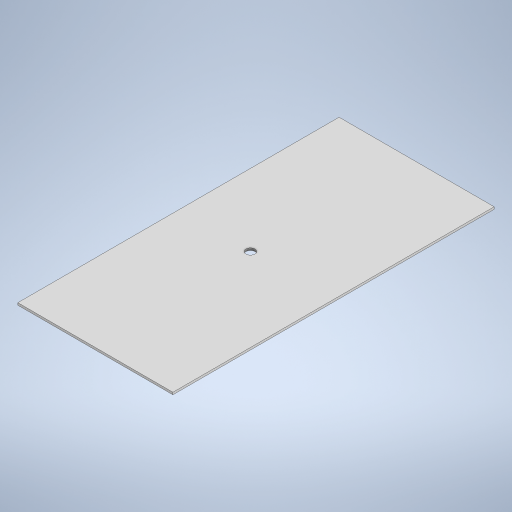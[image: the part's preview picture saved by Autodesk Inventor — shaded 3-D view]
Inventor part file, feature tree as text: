
AUTODESK INVENTOR PART (.ipt)
format: ipt  version: 2023 (Build 270158000, 158)  size: 218,624 bytes
history: native  units: mm
features: other x1, extrude x1, sketch x1
ambient origin geometry x8: Origin, YZ Plane, XZ Plane, XY Plane, X Axis, Y Axis, Z Axis, Center Point
bodies: Body1 (feature_tree)
feature tree (3):
  other  "Твердое тело1"
  extrude  "Выдавливание1"  Depth=280.0mm
  sketch  "Эскиз1"
